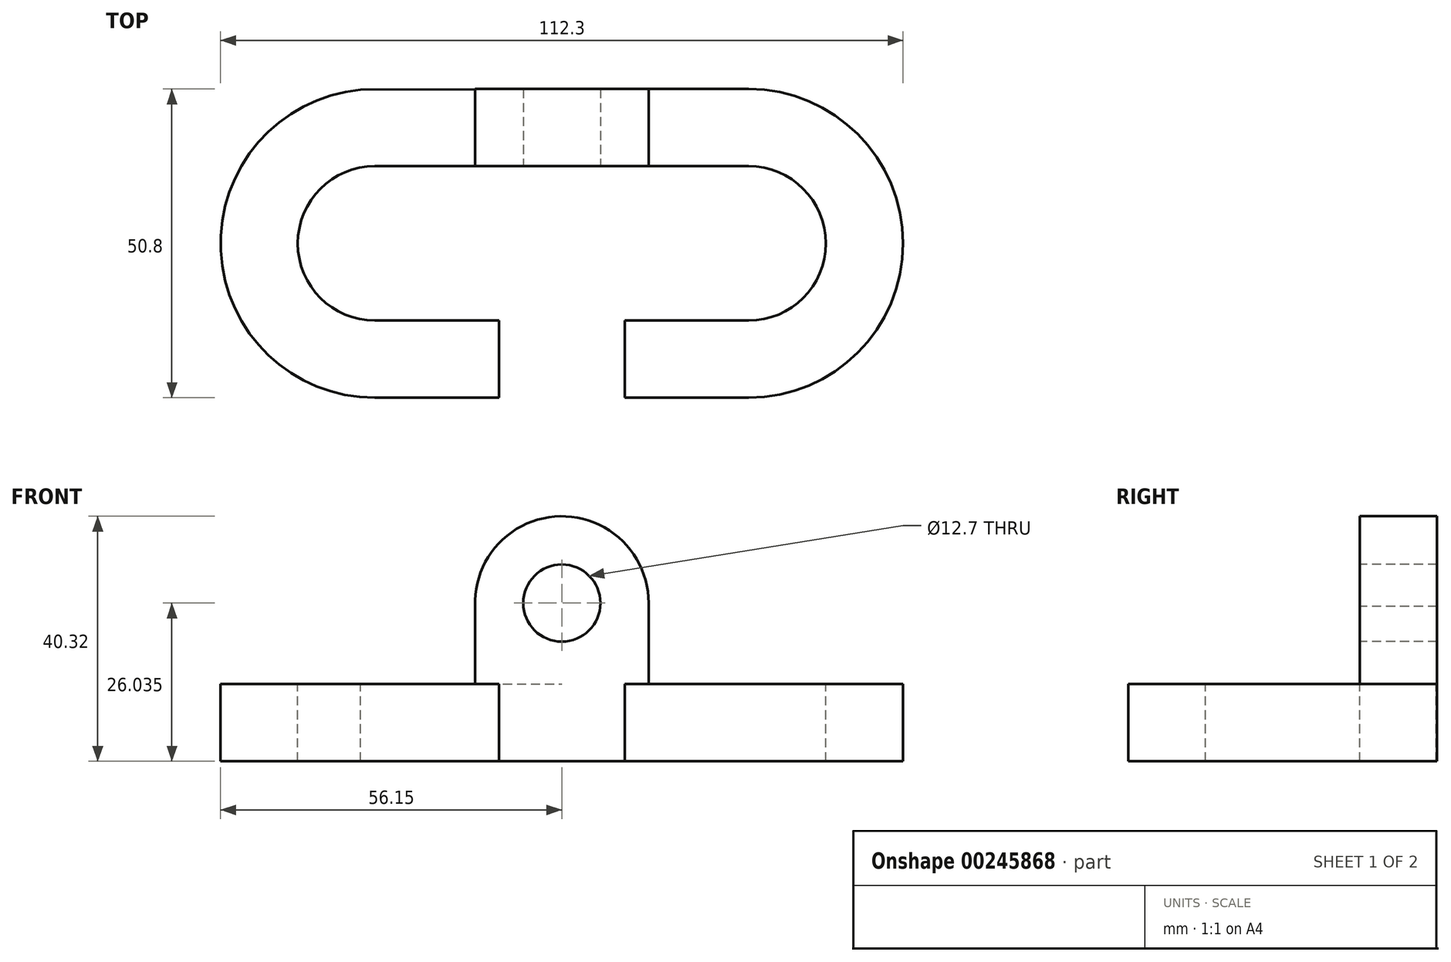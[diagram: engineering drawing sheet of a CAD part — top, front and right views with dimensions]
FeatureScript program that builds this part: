
annotation { "Feature Type Name" : "Feature", "Feature Type Description" : "" }
export const myFeature = defineFeature(function(context is Context, id is Id, definition is map)
    precondition{}
    {
        {
            var Q0;
            Q0=qCreatedBy(makeId("Top.planeOp"),FACE);
            var sketch = newSketch(context, id + "F0", { "sketchPlane" : qUnion([Q0])});
            skArc(sketch, "E0", {"start": v(30.75, -12.7) * mm, "mid": v(43.45, 0) * mm, "end": v(30.75, 12.7) * mm});
            skArc(sketch, "E1", {"start": v(30.75, -25.4) * mm, "mid": v(56.15, 0) * mm, "end": v(30.75, 25.4) * mm});
            skLineSegment(sketch, "E2", {"start": v(30.75, 0) * mm, "end": v(30.75, 55.52) * mm, "construction": true});
            skLineSegment(sketch, "E3", {"start": v(30.75, 25.4) * mm, "end": v(30.75, 12.7) * mm, "construction": true});
            skLineSegment(sketch, "E4", {"start": v(30.75, 12.7) * mm, "end": v(30.75, 25.4) * mm});
            skLineSegment(sketch, "E5", {"start": v(30.75, -12.7) * mm, "end": v(10.34, -12.7) * mm});
            skLineSegment(sketch, "E6", {"start": v(10.34, -12.7) * mm, "end": v(30.75, -12.7) * mm});
            skLineSegment(sketch, "E7", {"start": v(30.75, -25.4) * mm, "end": v(10.34, -25.4) * mm});
            skLineSegment(sketch, "E8", {"start": v(10.34, -25.4) * mm, "end": v(30.75, -25.4) * mm});
            skLineSegment(sketch, "E9", {"start": v(10.34, -12.7) * mm, "end": v(10.34, -25.4) * mm});
            skPoint(sketch, "E10.orphan", {"position": v(0, -25.4) * mm});
            skPoint(sketch, "E11.orphan", {"position": v(0, -12.7) * mm});
            skArc(sketch, "E12.MirrorCS", {"start": v(-30.75, -25.4) * mm, "mid": v(-56.15, 0) * mm, "end": v(-30.75, 25.4) * mm});
            skPoint(sketch, "E13.start.orphan", {"position": v(0, 25.4) * mm});
            skLineSegment(sketch, "E14", {"start": v(0, 25.4) * mm, "end": v(33.14, 25.29) * mm});
            skPoint(sketch, "E15.MirrorCS.end.orphan", {"position": v(30.75, 12.7) * mm});
            skPoint(sketch, "E15.MirrorCS.start.orphan", {"position": v(0, 12.7) * mm});
            skLineSegment(sketch, "E16", {"start": v(30.75, 12.7) * mm, "end": v(0, 12.7) * mm});
            skLineSegment(sketch, "E17", {"start": v(0, 25.4) * mm, "end": v(30.75, 25.4) * mm});
            skPoint(sketch, "E18.MirrorCS.end.orphan", {"position": v(-30.75, 25.4) * mm});
            skPoint(sketch, "E19.MirrorCS.end.orphan", {"position": v(-30.75, 12.7) * mm});
            skPoint(sketch, "E20.MirrorCS.end.orphan", {"position": v(-30.75, -12.7) * mm});
            skPoint(sketch, "E20.MirrorCS.start.orphan", {"position": v(-10.34, -12.7) * mm});
            skLineSegment(sketch, "E21.MirrorCS", {"start": v(30.84, 37.9) * mm, "end": v(0.09, 38.1) * mm});
            skLineSegment(sketch, "E22.MirrorCS", {"start": v(0, 25.4) * mm, "end": v(-33.14, 25.29) * mm});
            skLineSegment(sketch, "E23.MirrorCS", {"start": v(-30.75, 12.7) * mm, "end": v(0, 12.7) * mm});
            skLineSegment(sketch, "E24.MirrorCS", {"start": v(-10.34, -12.7) * mm, "end": v(-30.75, -12.7) * mm});
            skLineSegment(sketch, "E25.MirrorCS", {"start": v(-10.34, -25.4) * mm, "end": v(-30.75, -25.4) * mm});
            skLineSegment(sketch, "E26.MirrorCS", {"start": v(-10.34, -12.7) * mm, "end": v(-10.34, -25.4) * mm});
            skArc(sketch, "E27.MirrorCS", {"start": v(-30.75, -12.7) * mm, "mid": v(-43.45, 0) * mm, "end": v(-30.75, 12.7) * mm});
            skSolve(sketch);
        }
        {
            var Q0;
            Q0 = qSketchRegion(id + "F0", true);
            extrude(context, id + "F1", {"entities" : qUnion([Q0]), "oppositeDirection" : true, "depth" : 12.7 * mm});
        }
        {
            var Q0;
            Q0=makeQuery(id+"F1.opExtrude","SWEPT_FACE",FACE,{"disambiguationData":[OSD([sQuery(id+"F0.wireOp",EDGE,"E16"),sQuery(id+"F0.wireOp",EDGE,"E23.MirrorCS")])]});
            var sketch = newSketch(context, id + "F2", { "sketchPlane" : qUnion([Q0])});
            skCircle(sketch, "E28", {"center": v(0, 13.34) * mm, "radius": 6.35 * mm});
            skArc(sketch, "E29", {"start": v(14.29, 13.34) * mm, "mid": v(-0.26, 27.62) * mm, "end": v(-14.28, 12.8) * mm});
            skLineSegment(sketch, "E30", {"start": v(-14.28, 12.8) * mm, "end": v(-14.28, 0) * mm});
            skPoint(sketch, "E30.endSnap0", {"position": v(0, 0) * mm});
            skLineSegment(sketch, "E31", {"start": v(-14.28, 0) * mm, "end": v(-14.28, 12.8) * mm});
            skLineSegment(sketch, "E32", {"start": v(14.29, 13.34) * mm, "end": v(14.29, 0) * mm});
            skLineSegment(sketch, "E33", {"start": v(14.29, 0) * mm, "end": v(14.29, 13.34) * mm});
            skSolve(sketch);
        }
        {
            var Q0;
            Q0=makeQuery(id+"F2.imprint","IMPRINT",FACE,{"disambiguationData":[TD([[makeQuery(id+"F2.imprint","IMPRINT",EDGE,{"derivedFrom":sQuery(id+"F2.wireOp",EDGE,"E28")}),-1.0]])]});
            extrude(context, id + "F3", {"entities" : qUnion([Q0]), "operationType" : NewBodyOperationType.ADD, "oppositeDirection" : true, "depth" : 12.7 * mm});
        }
    });
